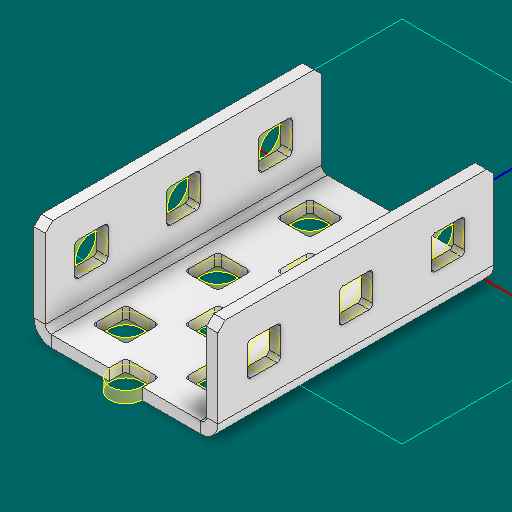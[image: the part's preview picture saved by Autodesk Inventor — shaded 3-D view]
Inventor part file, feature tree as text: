
AUTODESK INVENTOR PART (.ipt)
format: ipt  version: 2025 (Build 290162000, 162)  size: 418,304 bytes
history: native  units: in
note: dims shown in document units (in); Inventor stores cm internally (conversion verified against a paired STEP export)
features: other x36, sketch x5, sheet_metal_op x1
ambient origin geometry x8: Origin, YZ Plane, XZ Plane, XY Plane, X Axis, Y Axis, Z Axis, Center Point
bodies: Solid1 (feature_tree)
feature tree (42):
  other  "Alu C 1x2x1x3.ipt"
  other  "Solid1::Alu C 1x2x1x3.ipt"
  other  "TaggingFeature1"
  sketch  "Sketch1"  dims[d0=0.3937in]
  sketch  "Sketch2"  dims[d1=0.0625in]
  sketch  "Sketch3"
  other  "Flange Pattern Sketch"
  sketch  "Sketch9"
  sheet_metal_op  "Body Pattern Sketch"
  other  "Arc Length"
  sketch  "Sketch14"
  other  "Flange Pattern Plane"
  other  "Srf1"
  other  "Srf2"
  other  "Srf3"
  other  "Srf4"
  other  "Srf5"
  other  "Srf6"
  other  "Srf7"
  other  "Srf8"
  other  "Srf9"
  other  "Srf10"
  other  "Srf11"
  other  "Srf12"
  other  "Srf13"
  other  "Srf14"
  other  "Srf15"
  other  "Srf1::Derived"
  other  "Srf2::Derived"
  other  "Srf823::Derived"
  other  "Srf824::Derived"
  other  "Srf825::Derived"
  other  "Srf826::Derived"
  other  "Srf91::Derived"
  other  "Srf92::Derived"
  other  "Srf856::Derived"
  other  "Srf857::Derived"
  other  "Srf858::Derived"
  other  "Srf859::Derived"
  other  "Srf786::Derived"
  other  "Srf889::Derived"
  other  "Srf890::Derived"
